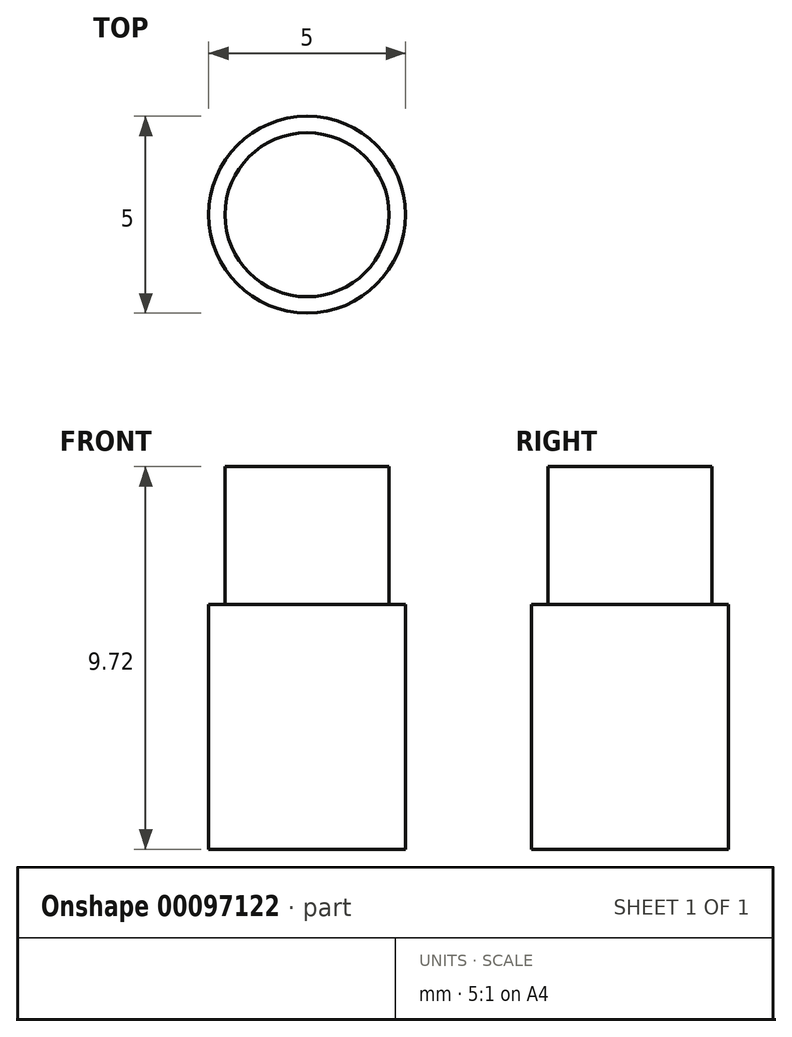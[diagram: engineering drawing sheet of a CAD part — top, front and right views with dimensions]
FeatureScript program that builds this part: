
annotation { "Feature Type Name" : "Feature", "Feature Type Description" : "" }
export const myFeature = defineFeature(function(context is Context, id is Id, definition is map)
    precondition{}
    {
        {
            var Q0;
            Q0=qCreatedBy(makeId("Front.planeOp"),FACE);
            var sketch = newSketch(context, id + "F0", { "sketchPlane" : qUnion([Q0])});
            skLineSegment(sketch, "E0", {"start": v(0, 0) * mm, "end": v(-2.5, 0) * mm});
            skLineSegment(sketch, "E1", {"start": v(-2.5, 0) * mm, "end": v(-2.5, 6.22) * mm});
            skLineSegment(sketch, "E2", {"start": v(-2.5, 6.22) * mm, "end": v(-2.08, 6.22) * mm});
            skLineSegment(sketch, "E3", {"start": v(-2.08, 6.22) * mm, "end": v(-2.08, 9.72) * mm});
            skLineSegment(sketch, "E4", {"start": v(-2.08, 9.72) * mm, "end": v(0, 9.72) * mm});
            skLineSegment(sketch, "E5", {"start": v(0, 9.72) * mm, "end": v(0, 0) * mm});
            skSolve(sketch);
        }
        {
            var Q0;
            Q0 = qSketchRegion(id + "F0", true);
            var Q1;
            Q1=sQuery(id+"F0.wireOp",EDGE,"E5");
            revolve(context, id + "F1", {"entities" : qUnion([Q0]), "axis" : qUnion([Q1]), "revolveType" : RevolveType.FULL});
        }
    });
